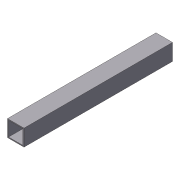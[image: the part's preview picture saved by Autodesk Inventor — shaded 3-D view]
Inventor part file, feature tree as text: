
AUTODESK INVENTOR PART (.ipt)
format: ipt  version: 2012 (Build 160160000, 160)  size: 71,168 bytes
history: native  units: in
note: dims shown in document units (in); Inventor stores cm internally (conversion verified against a paired STEP export)
features: extrude x1, shell x1, sketch x1
ambient origin geometry x8: Origin, YZ Plane, XZ Plane, XY Plane, X Axis, Y Axis, Z Axis, Center Point
bodies: Solid1 (feature_tree)
feature tree (3):
  extrude  "Extrusion1"  Depth=1.0in
  shell  "Shell1"  Thickness=9.0in
  sketch  "Sketch1"  dims[d0=1.0in d1=1.0in d2=9.0in d3=0.0in d4=0.0625in]
